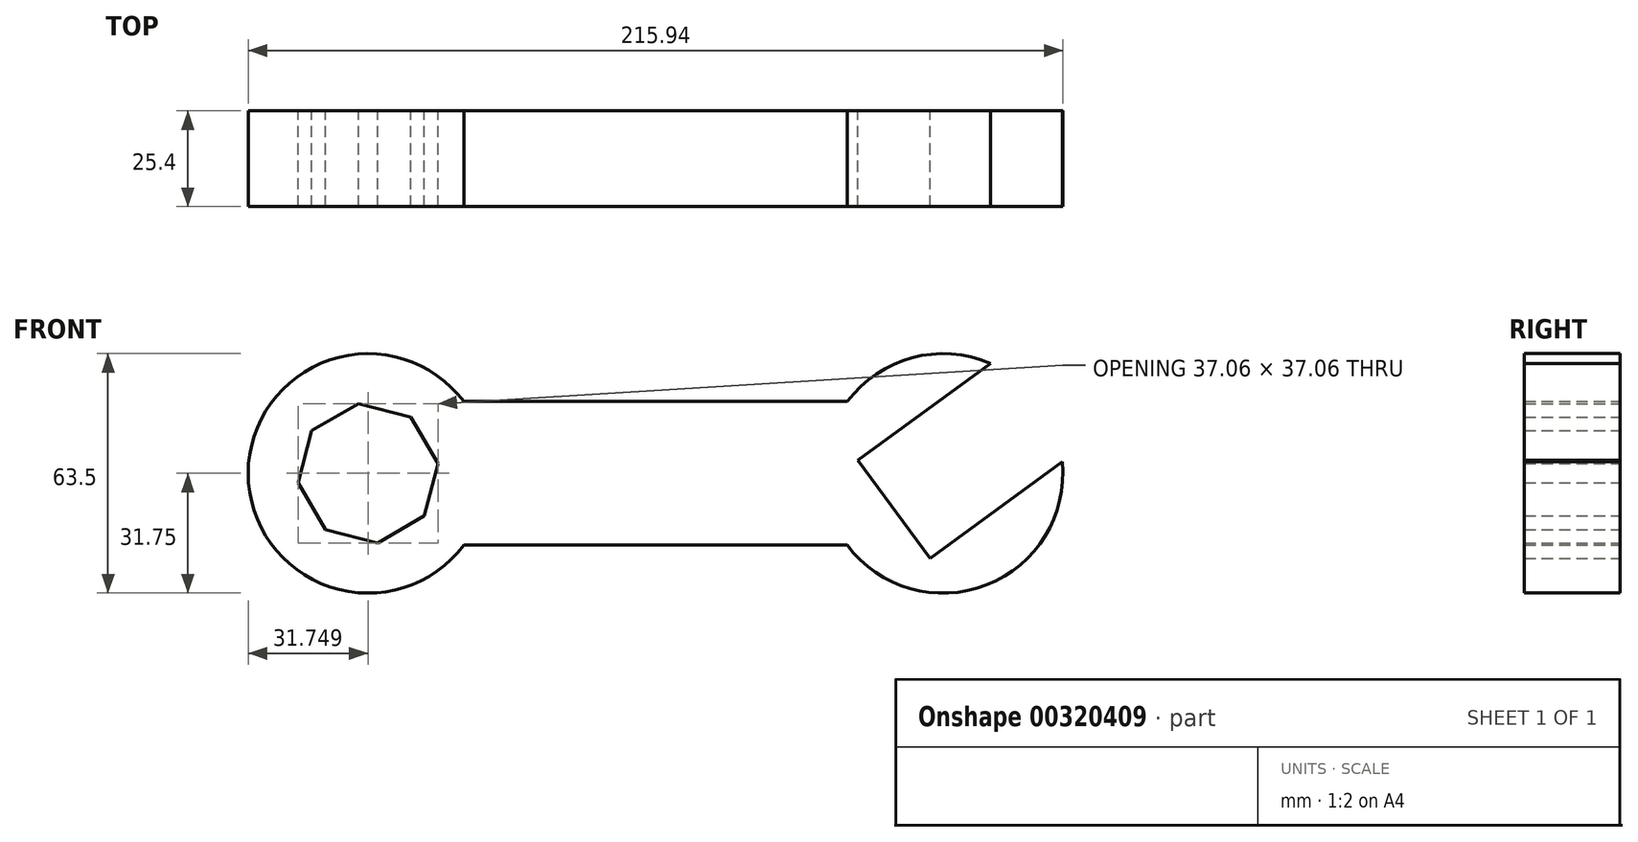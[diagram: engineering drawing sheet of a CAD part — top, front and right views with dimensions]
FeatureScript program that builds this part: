
annotation { "Feature Type Name" : "Feature", "Feature Type Description" : "" }
export const myFeature = defineFeature(function(context is Context, id is Id, definition is map)
    precondition{}
    {
        {
            var Q0;
            Q0=qCreatedBy(makeId("Front.planeOp"),FACE);
            var sketch = newSketch(context, id + "F0", { "sketchPlane" : qUnion([Q0])});
            skCircle(sketch, "E0", {"center": v(-76.2, 0) * mm, "radius": 31.75 * mm});
            skArc(sketch, "E1", {"start": v(88.77, 29.18) * mm, "mid": v(50.64, -18.76) * mm, "end": v(107.85, 3.13) * mm});
            skLineSegment(sketch, "E2", {"start": v(-50.8, 19.05) * mm, "end": v(50.85, 19.05) * mm});
            skLineSegment(sketch, "E3", {"start": v(-76.2, 0) * mm, "end": v(76.25, 0) * mm, "construction": true});
            skLineSegment(sketch, "E4.MirrorCS", {"start": v(-50.8, -19.05) * mm, "end": v(50.85, -19.05) * mm});
            skCircle(sketch, "E5.cCircle", {"center": v(-76.2, 0) * mm, "radius": 17.28 * mm, "construction": true});
            skLineSegment(sketch, "E5.0", {"start": v(-64.88, 14.9) * mm, "end": v(-57.66, 2.54) * mm});
            skLineSegment(sketch, "E5.1", {"start": v(-57.66, 2.54) * mm, "end": v(-61.3, -11.3) * mm});
            skLineSegment(sketch, "E5.2", {"start": v(-61.3, -11.3) * mm, "end": v(-73.65, -18.53) * mm});
            skLineSegment(sketch, "E5.3", {"start": v(-73.65, -18.53) * mm, "end": v(-87.5, -14.9) * mm});
            skLineSegment(sketch, "E5.4", {"start": v(-87.5, -14.9) * mm, "end": v(-94.72, -2.54) * mm});
            skLineSegment(sketch, "E5.5", {"start": v(-94.72, -2.54) * mm, "end": v(-91.09, 11.3) * mm});
            skLineSegment(sketch, "E5.6", {"start": v(-91.09, 11.3) * mm, "end": v(-78.73, 18.53) * mm});
            skLineSegment(sketch, "E5.7", {"start": v(-78.73, 18.53) * mm, "end": v(-64.88, 14.9) * mm});
            skPoint(sketch, "E5.0.midPoint", {"position": v(-61.27, 8.72) * mm});
            skCircle(sketch, "E6.cCircle", {"center": v(76.25, 0) * mm, "radius": 16.14 * mm, "construction": true});
            skLineSegment(sketch, "E6.1", {"start": v(98.81, -3.48) * mm, "end": v(72.77, -22.56) * mm});
            skLineSegment(sketch, "E6.2", {"start": v(72.77, -22.56) * mm, "end": v(53.69, 3.48) * mm});
            skLineSegment(sketch, "E6.3", {"start": v(53.69, 3.48) * mm, "end": v(79.74, 22.56) * mm});
            skPoint(sketch, "E6.0.midPoint", {"position": v(89.27, 9.54) * mm});
            skLineSegment(sketch, "E7", {"start": v(79.74, 22.56) * mm, "end": v(88.77, 29.18) * mm});
            skLineSegment(sketch, "E8", {"start": v(98.81, -3.48) * mm, "end": v(107.85, 3.13) * mm});
            skSolve(sketch);
        }
        {
            var Q0;
            Q0 = qSketchRegion(id + "F0", true);
            extrude(context, id + "F1", {"entities" : qUnion([Q0]), "depth" : 25.4 * mm});
        }
    });
